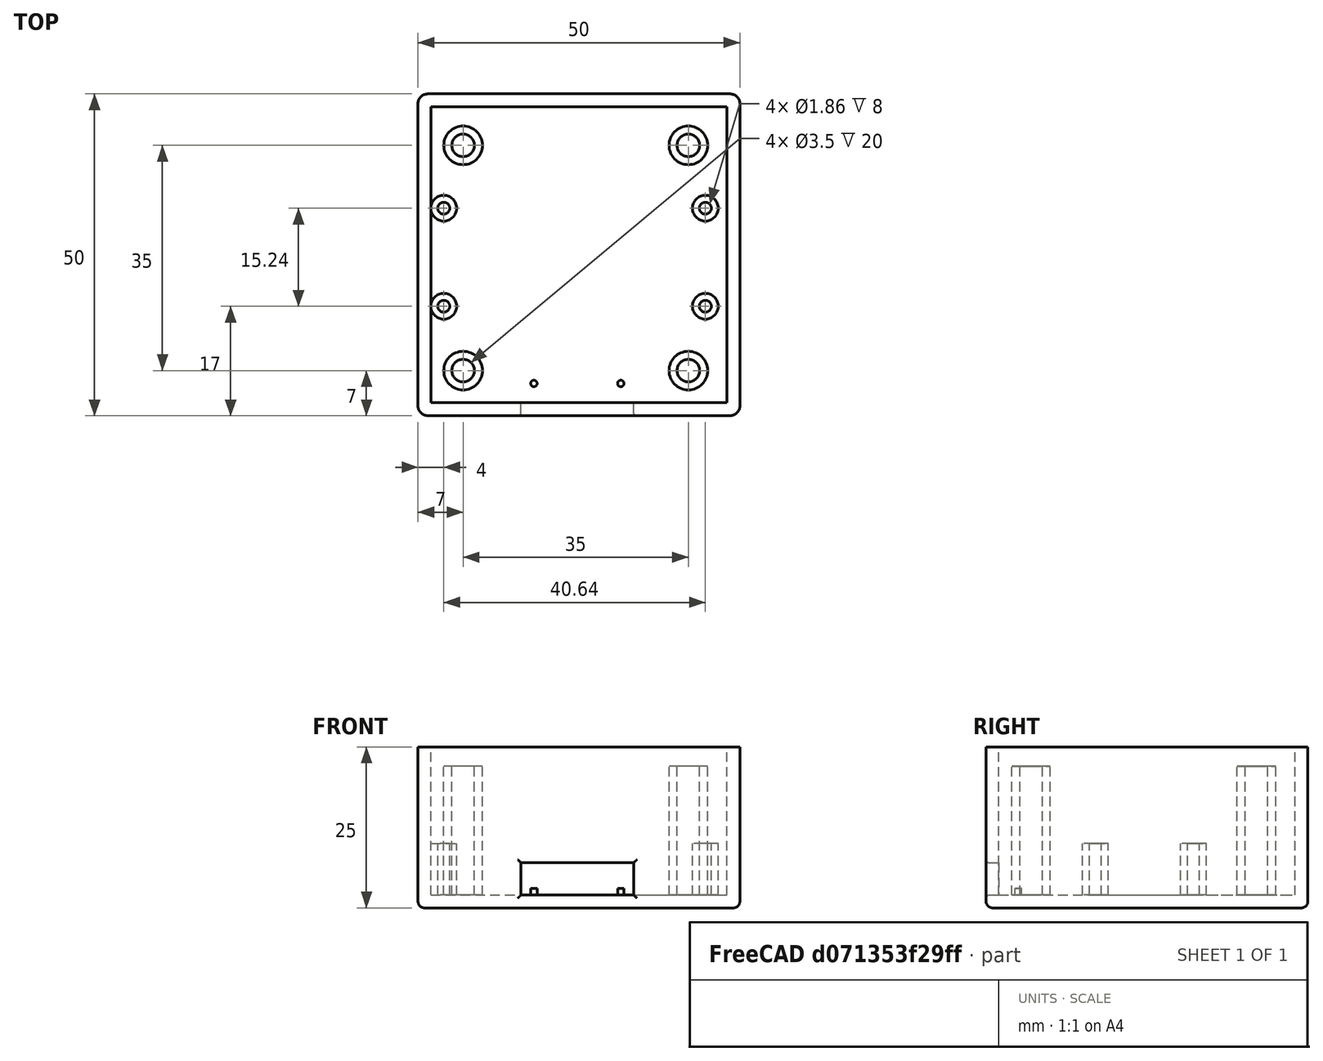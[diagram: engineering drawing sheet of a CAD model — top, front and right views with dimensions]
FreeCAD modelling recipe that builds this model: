
FCSTD DOCUMENT  (FreeCAD 0.18R4 (GitTag))
Label: PT_Bottom
License: All rights reserved
LicenseURL: http://en.wikipedia.org/wiki/All_rights_reserved
objects: Part::Cylinder×18, Part::Cut×10, Part::Fuse×10, Part::Box×3, Part::Fillet×3, App::DocumentObjectGroup×1
note: 44 computed .brp shape members not serialized (recipe doc carries the construction recipe); baked Part::Feature solids carry a one-line shape summary decoded from their .brp

FEATURE [Part::Box] Box  label="50x40x15"
  AttacherType = Attacher::AttachEngine3D
  Height = 25
  Length = 50
  Width = 50
FEATURE [Part::Box] Box001  label="46x36x15"
  AttacherType = Attacher::AttachEngine3D
  Height = 25
  Length = 46
  Placement = pos=(2,2,2) rot=(0,0,1;0rad)
  Width = 46
FEATURE [Part::Cut] Cut
  Base = -> Box
  Tool = -> Box001
FEATURE [Part::Cylinder] Cylinder  label="Sylinteri"
  Angle = 360
  AttacherType = Attacher::AttachEngine3D
  Height = 10
  Placement = pos=(7,10,0) rot=(0,0,1;0rad)
  Radius = 2
FEATURE [Part::Cylinder] Cylinder001  label="Sylinteri001"
  Angle = 360
  AttacherType = Attacher::AttachEngine3D
  Height = 10
  Placement = pos=(7,10,2) rot=(0,0,1;0rad)
  Radius = 0.93
FEATURE [Part::Cut] Cut001  label="NanoPlatorm"
  Base = -> Cylinder
  Placement = pos=(-3,-1,0) rot=(0,0,1;0rad)
  Tool = -> Cylinder001
FEATURE [Part::Cylinder] Cylinder002  label="Sylinteri002"
  Angle = 360
  AttacherType = Attacher::AttachEngine3D
  Height = 10
  Placement = pos=(7,10,0) rot=(0,0,1;0rad)
  Radius = 2
FEATURE [Part::Cylinder] Cylinder003  label="Sylinteri003"
  Angle = 360
  AttacherType = Attacher::AttachEngine3D
  Height = 10
  Placement = pos=(7,10,2) rot=(0,0,1;0rad)
  Radius = 0.93
FEATURE [Part::Cut] Cut002  label="NanoPlatorm001"
  Base = -> Cylinder002
  Placement = pos=(-3,14.24,0) rot=(0,0,1;0rad)
  Tool = -> Cylinder003
FEATURE [Part::Cylinder] Cylinder004  label="Sylinteri004"
  Angle = 360
  AttacherType = Attacher::AttachEngine3D
  Height = 10
  Placement = pos=(7,10,0) rot=(0,0,1;0rad)
  Radius = 2
FEATURE [Part::Cylinder] Cylinder005  label="Sylinteri005"
  Angle = 360
  AttacherType = Attacher::AttachEngine3D
  Height = 10
  Placement = pos=(7,10,2) rot=(0,0,1;0rad)
  Radius = 0.93
FEATURE [Part::Cut] Cut003  label="NanoPlatorm002"
  Base = -> Cylinder004
  Placement = pos=(37.64,-1,0) rot=(0,0,1;0rad)
  Tool = -> Cylinder005
FEATURE [Part::Cylinder] Cylinder006  label="Sylinteri006"
  Angle = 360
  AttacherType = Attacher::AttachEngine3D
  Height = 10
  Placement = pos=(7,10,2) rot=(0,0,1;0rad)
  Radius = 0.93
FEATURE [Part::Cylinder] Cylinder007  label="Sylinteri007"
  Angle = 360
  AttacherType = Attacher::AttachEngine3D
  Height = 10
  Placement = pos=(7,10,0) rot=(0,0,1;0rad)
  Radius = 2
FEATURE [Part::Cut] Cut004  label="NanoPlatorm003"
  Base = -> Cylinder007
  Placement = pos=(37.64,14.24,0) rot=(0,0,1;0rad)
  Tool = -> Cylinder006
FEATURE [Part::Fuse] Fusion
  Base = -> Cut001
  Tool = -> Cut002
FEATURE [Part::Fuse] Fusion001
  Base = -> Cut003
  Tool = -> Cut004
FEATURE [Part::Fuse] Fusion002  label="NanoPlatform"
  Base = -> Fusion
  Placement = pos=(0,8,0) rot=(0,0,1;0rad)
  Tool = -> Fusion001
FEATURE [Part::Box] Box002  label="Cube"
  AttacherType = Attacher::AttachEngine3D
  Height = 5
  Length = 17.5
  Placement = pos=(16,0,2) rot=(0,0,1;0rad)
  Width = 10
FEATURE [Part::Fuse] Fusion003
  Base = -> Cut
  Tool = -> Fusion002
FEATURE [Part::Cut] Cut005
  Base = -> Fusion003
  Tool = -> Box002
FEATURE [Part::Cylinder] Cylinder008  label="Cylinder"
  Angle = 360
  AttacherType = Attacher::AttachEngine3D
  Height = 2
  Radius = 0.5
FEATURE [Part::Cylinder] Cylinder009  label="Cylinder001"
  Angle = 360
  AttacherType = Attacher::AttachEngine3D
  Height = 2
  Placement = pos=(13.5,0,0) rot=(0,0,1;0rad)
  Radius = 0.5
FEATURE [Part::Fuse] Fusion004
  Base = -> Cylinder008
  Placement = pos=(18,5,1) rot=(0,0,1;0rad)
  Tool = -> Cylinder009
FEATURE [Part::Cylinder] Cylinder010  label="Cylinder002"
  Angle = 360
  AttacherType = Attacher::AttachEngine3D
  Height = 22
  Radius = 3
FEATURE [Part::Cylinder] Cylinder011  label="Cylinder003"
  Angle = 360
  AttacherType = Attacher::AttachEngine3D
  Height = 22
  Radius = 1.75
FEATURE [Part::Cut] Cut006
  Base = -> Cylinder010
  Placement = pos=(6,35,0) rot=(0,0,1;0rad)
  Tool = -> Cylinder011
FEATURE [Part::Cylinder] Cylinder012  label="Cylinder004"
  Angle = 360
  AttacherType = Attacher::AttachEngine3D
  Height = 22
  Radius = 3
FEATURE [Part::Cylinder] Cylinder013  label="Cylinder005"
  Angle = 360
  AttacherType = Attacher::AttachEngine3D
  Height = 22
  Radius = 1.75
FEATURE [Part::Cut] Cut007
  Base = -> Cylinder012
  Placement = pos=(41,35,0) rot=(0,0,1;0rad)
  Tool = -> Cylinder013
FEATURE [Part::Fuse] Fusion005
  Base = -> Cut006
  Tool = -> Cut007
FEATURE [Part::Fuse] Fusion006
  Base = -> Cut005
  Tool = -> Fusion004
FEATURE [Part::Cylinder] Cylinder014  label="Cylinder006"
  Angle = 360
  AttacherType = Attacher::AttachEngine3D
  Height = 22
  Radius = 3
FEATURE [Part::Cylinder] Cylinder015  label="Cylinder007"
  Angle = 360
  AttacherType = Attacher::AttachEngine3D
  Height = 22
  Radius = 1.75
FEATURE [Part::Cut] Cut009
  Base = -> Cylinder014
  Placement = pos=(6,35,0) rot=(0,0,1;0rad)
  Tool = -> Cylinder015
FEATURE [Part::Cylinder] Cylinder016  label="Cylinder008"
  Angle = 360
  AttacherType = Attacher::AttachEngine3D
  Height = 22
  Radius = 1.75
FEATURE [Part::Cylinder] Cylinder017  label="Cylinder009"
  Angle = 360
  AttacherType = Attacher::AttachEngine3D
  Height = 22
  Radius = 3
FEATURE [Part::Cut] Cut008
  Base = -> Cylinder017
  Placement = pos=(41,35,0) rot=(0,0,1;0rad)
  Tool = -> Cylinder016
FEATURE [Part::Fuse] Fusion007
  Base = -> Cut009
  Placement = pos=(0,-35,0) rot=(0,0,1;0rad)
  Tool = -> Cut008
FEATURE [Part::Fuse] Fusion008  label="PCB_Platform"
  Base = -> Fusion005
  Placement = pos=(1,7,0) rot=(0,0,1;0rad)
  Tool = -> Fusion007
FEATURE [Part::Fuse] Fusion009
  Base = -> Fusion006
  Tool = -> Fusion008
FEATURE [App::DocumentObjectGroup] Group  label="Bottom"
  Group = -> [Fusion009]
FEATURE [Part::Fillet] Fillet
  Base = -> Fusion009
  Edges = 4 edges r=1.5: [Edge1,Edge3,Edge6,Edge19]
FEATURE [Part::Fillet] Fillet001
  Base = -> Fillet
  Edges = 8 edges r=1: [Edge4,Edge16,Edge18,Edge20,Edge21,Edge22,Edge23,Edge24]
FEATURE [Part::Fillet] Fillet002
  Base = -> Fillet001
  Edges = 4 edges r=0.5: [Edge27,Edge28,Edge29,Edge30]
